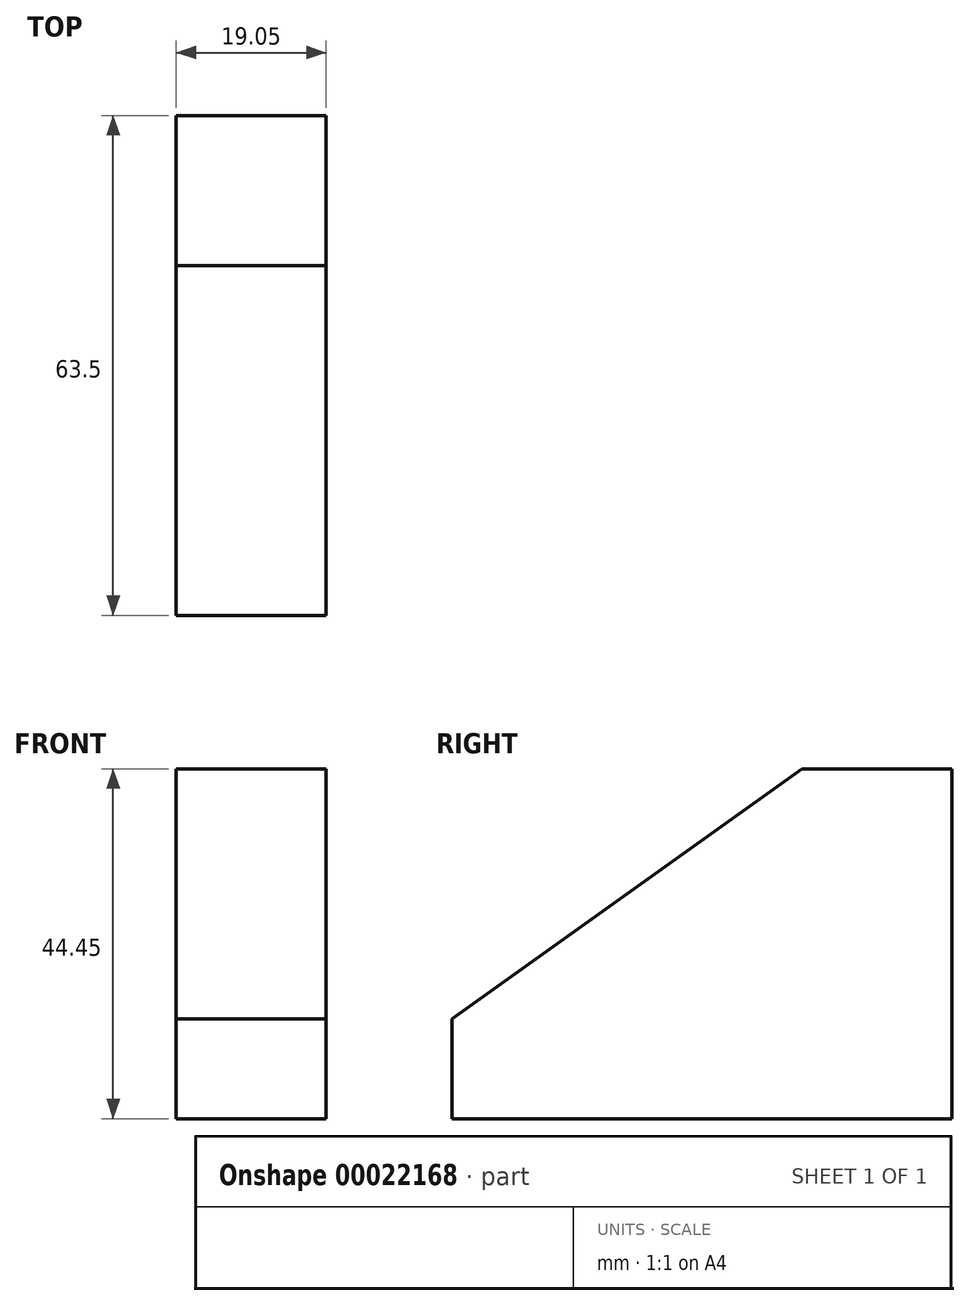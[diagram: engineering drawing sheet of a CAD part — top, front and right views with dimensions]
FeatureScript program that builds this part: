
annotation { "Feature Type Name" : "Feature", "Feature Type Description" : "" }
export const myFeature = defineFeature(function(context is Context, id is Id, definition is map)
    precondition{}
    {
        {
            var Q0;
            Q0=qCreatedBy(makeId("Right.planeOp"),FACE);
            var sketch = newSketch(context, id + "F0", { "sketchPlane" : qUnion([Q0])});
            skLineSegment(sketch, "E0", {"start": v(-77.58, -55.2) * mm, "end": v(-77.58, -67.9) * mm});
            skLineSegment(sketch, "E1", {"start": v(-77.58, -67.9) * mm, "end": v(-14.08, -67.9) * mm});
            skLineSegment(sketch, "E2", {"start": v(-14.08, -67.9) * mm, "end": v(-14.08, -23.45) * mm});
            skLineSegment(sketch, "E3", {"start": v(-14.08, -23.45) * mm, "end": v(-33.13, -23.45) * mm});
            skLineSegment(sketch, "E4", {"start": v(-33.13, -23.45) * mm, "end": v(-77.58, -55.2) * mm});
            skSolve(sketch);
        }
        {
            var Q0;
            Q0 = qSketchRegion(id + "F0", true);
            extrude(context, id + "F1", {"entities" : qUnion([Q0]), "depth" : 19.05 * mm});
        }
    });
